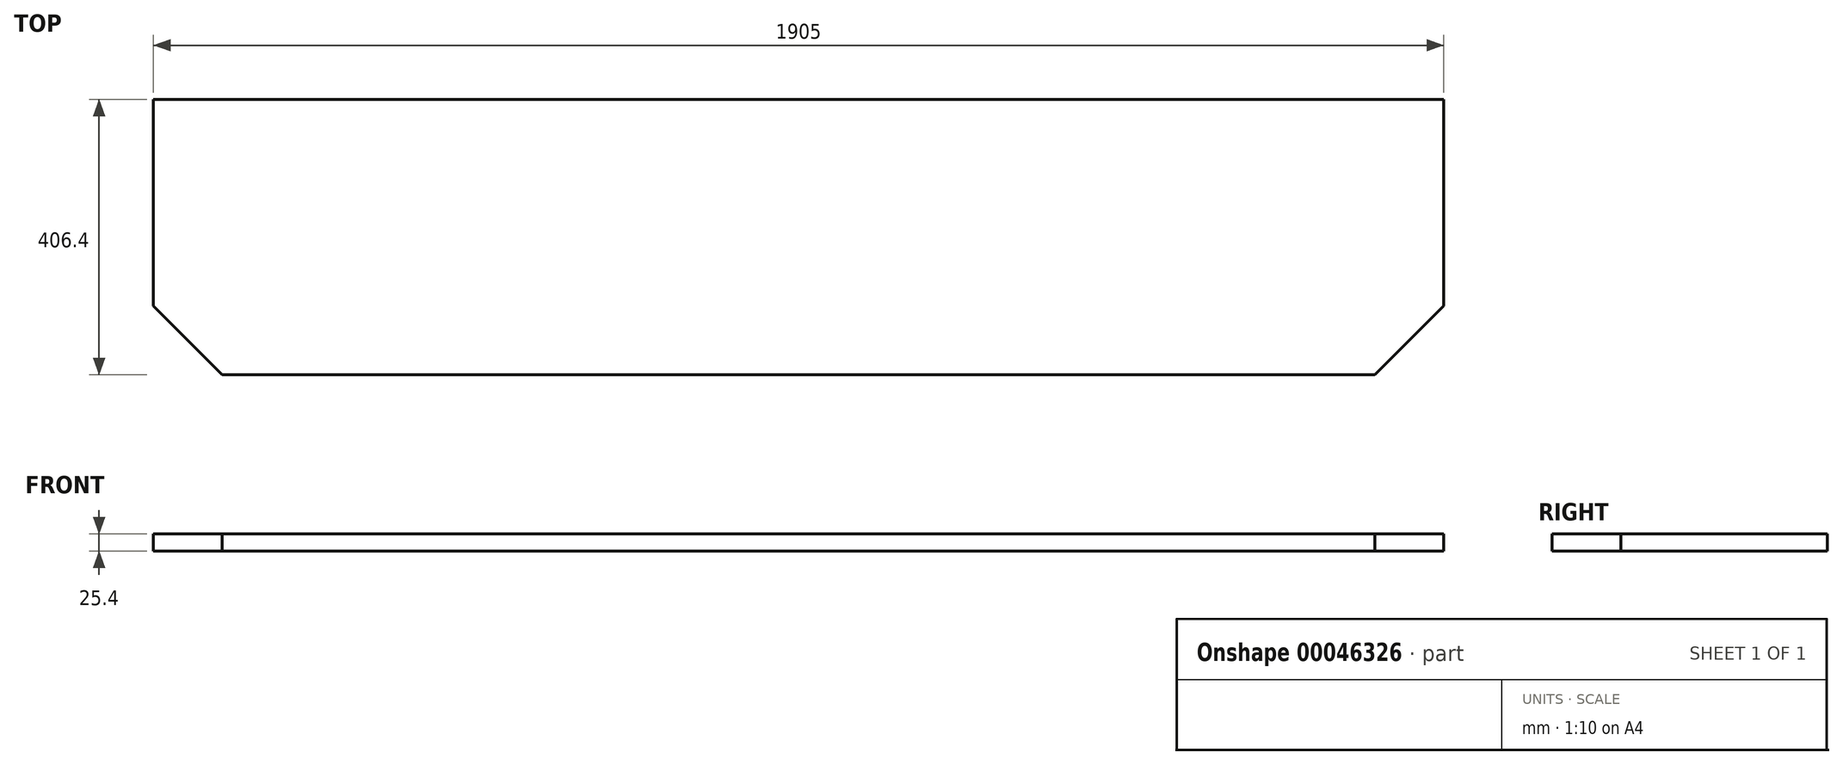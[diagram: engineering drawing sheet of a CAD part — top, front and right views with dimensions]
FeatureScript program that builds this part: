
annotation { "Feature Type Name" : "Feature", "Feature Type Description" : "" }
export const myFeature = defineFeature(function(context is Context, id is Id, definition is map)
    precondition{}
    {
        {
            var Q0;
            Q0=qCreatedBy(makeId("Top.planeOp"),FACE);
            var sketch = newSketch(context, id + "F0", { "sketchPlane" : qUnion([Q0])});
            skLineSegment(sketch, "E0.rect.top", {"start": v(952.5, 152.4) * mm, "end": v(-952.5, 152.4) * mm});
            skLineSegment(sketch, "E0.rect.left", {"start": v(952.5, -152.4) * mm, "end": v(952.5, 152.4) * mm});
            skLineSegment(sketch, "E0.rect.right", {"start": v(-952.5, -152.4) * mm, "end": v(-952.5, 152.4) * mm});
            skPoint(sketch, "E0.rect.middle", {"position": v(0, 0) * mm});
            skLineSegment(sketch, "E1.top", {"start": v(-850.9, -254) * mm, "end": v(850.9, -254) * mm});
            skLineSegment(sketch, "E2", {"start": v(-952.5, -152.4) * mm, "end": v(-850.9, -254) * mm});
            skLineSegment(sketch, "E3", {"start": v(850.9, -254) * mm, "end": v(952.5, -152.4) * mm});
            skLineSegment(sketch, "E4", {"start": v(-850.9, -254) * mm, "end": v(-850.9, -152.4) * mm});
            skLineSegment(sketch, "E5", {"start": v(-952.5, -152.4) * mm, "end": v(-850.9, -152.4) * mm});
            skSolve(sketch);
        }
        {
            var Q0;
            Q0=makeQuery(id+"F0.imprint","IMPRINT",FACE,{"disambiguationData":[TD([[makeQuery(id+"F0.imprint","IMPRINT",EDGE,{"derivedFrom":sQuery(id+"F0.wireOp",EDGE,"E0.rect.top")}),1.0]])]});
            var Q1;
            Q1=makeQuery(id+"F0.imprint","IMPRINT",FACE,{"disambiguationData":[TD([[makeQuery(id+"F0.imprint","IMPRINT",EDGE,{"derivedFrom":sQuery(id+"F0.wireOp",EDGE,"E2")}),1.0]])]});
            extrude(context, id + "F1", {"entities" : qUnion([Q0, Q1]), "endBound" : BoundingType.SYMMETRIC, "depth" : 25.4 * mm});
        }
    });
